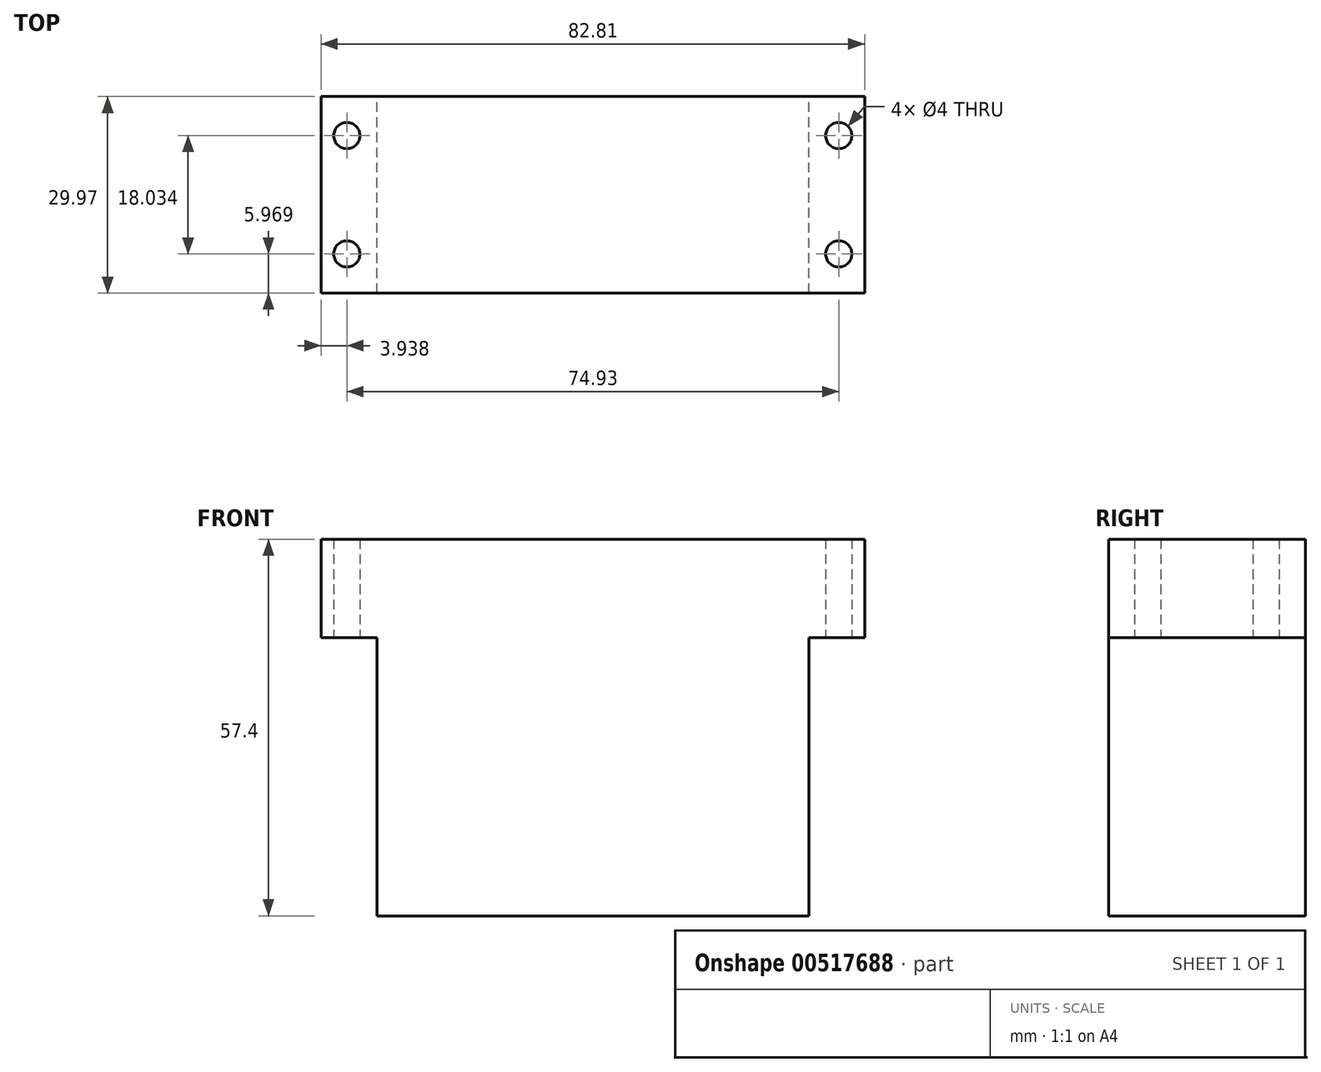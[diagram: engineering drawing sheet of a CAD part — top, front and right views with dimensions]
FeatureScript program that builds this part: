
annotation { "Feature Type Name" : "Feature", "Feature Type Description" : "" }
export const myFeature = defineFeature(function(context is Context, id is Id, definition is map)
    precondition{}
    {
        {
            var Q0;
            Q0=qCreatedBy(makeId("Top.planeOp"),FACE);
            var sketch = newSketch(context, id + "F0", { "sketchPlane" : qUnion([Q0])});
            skLineSegment(sketch, "E0.bottom", {"start": v(0, 0) * mm, "end": v(65.79, 0) * mm});
            skLineSegment(sketch, "E0.top", {"start": v(0, 29.97) * mm, "end": v(65.79, 29.97) * mm});
            skLineSegment(sketch, "E0.left", {"start": v(0, 0) * mm, "end": v(0, 29.97) * mm});
            skLineSegment(sketch, "E0.right", {"start": v(65.79, 0) * mm, "end": v(65.79, 29.97) * mm});
            skSolve(sketch);
        }
        {
            var Q0;
            Q0=makeQuery(id+"F0.imprint","IMPRINT",FACE,{"disambiguationData":[TD([[makeQuery(id+"F0.imprint","IMPRINT",EDGE,{"derivedFrom":sQuery(id+"F0.wireOp",EDGE,"E0.bottom")}),1.0]])]});
            extrude(context, id + "F1", {"entities" : qUnion([Q0]), "depth" : 42.42 * mm, "offsetDistance" : 25 * mm});
        }
        {
            var Q0;
            Q0=makeQuery(id+"F1.opExtrude","CAP_FACE",FACE,{"disambiguationData":[OSD([sQuery(id+"F0.wireOp",EDGE,"E0.bottom"),sQuery(id+"F0.wireOp",EDGE,"E0.top"),sQuery(id+"F0.wireOp",EDGE,"E0.left"),sQuery(id+"F0.wireOp",EDGE,"E0.right")])],"isStart":false});
            var sketch = newSketch(context, id + "F2", { "sketchPlane" : qUnion([Q0])});
            skLineSegment(sketch, "E1.bottom", {"start": v(-8.5, 29.97) * mm, "end": v(32.9, 29.97) * mm});
            skLineSegment(sketch, "E1.top", {"start": v(-8.5, 0) * mm, "end": v(32.9, 0) * mm});
            skLineSegment(sketch, "E1.left", {"start": v(-8.5, 29.97) * mm, "end": v(-8.5, 0) * mm});
            skCircle(sketch, "E2", {"center": v(-4.57, 5.97) * mm, "radius": 2 * mm});
            skLineSegment(sketch, "E3", {"start": v(32.9, 29.97) * mm, "end": v(32.9, 0) * mm, "construction": true});
            skLineSegment(sketch, "E4.MirrorCS", {"start": v(74.3, 29.97) * mm, "end": v(32.9, 29.97) * mm});
            skLineSegment(sketch, "E5.MirrorCS", {"start": v(74.3, 0) * mm, "end": v(32.9, 0) * mm});
            skCircle(sketch, "E6.MirrorC", {"center": v(70.36, 5.97) * mm, "radius": 2 * mm});
            skLineSegment(sketch, "E7.MirrorCS", {"start": v(74.3, 29.97) * mm, "end": v(74.3, 0) * mm});
            skLineSegment(sketch, "E8", {"start": v(32.9, 14.99) * mm, "end": v(74.3, 14.99) * mm, "construction": true});
            skCircle(sketch, "E9.MirrorC", {"center": v(-4.57, 24) * mm, "radius": 2 * mm});
            skCircle(sketch, "E10.MirrorC", {"center": v(70.36, 24) * mm, "radius": 2 * mm});
            skSolve(sketch);
        }
        {
            var Q0;
            Q0 = qSketchRegion(id + "F2", true);
            extrude(context, id + "F3", {"entities" : qUnion([Q0]), "operationType" : NewBodyOperationType.ADD, "depth" : 15 * mm, "offsetDistance" : 25 * mm});
        }
    });
